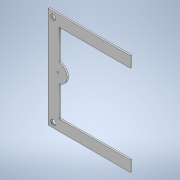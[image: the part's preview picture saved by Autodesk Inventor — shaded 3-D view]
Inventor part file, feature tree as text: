
AUTODESK INVENTOR PART (.ipt)
format: ipt  version: 2022 (Build 260153000, 153)  size: 114,176 bytes
history: native  units: mm
features: other x1, extrude x1, sketch x1
ambient origin geometry x8: Origin, YZ Plane, XZ Plane, XY Plane, X Axis, Y Axis, Z Axis, Center Point
bodies: Body1 (feature_tree)
feature tree (3):
  other  "Sólido1"
  extrude  "Extrusión1"  Depth=2.0mm TaperAngle=0.0deg
  sketch  "Boceto1"  dims[d0=2.0mm d1=2.0mm d2=0.0mm]
